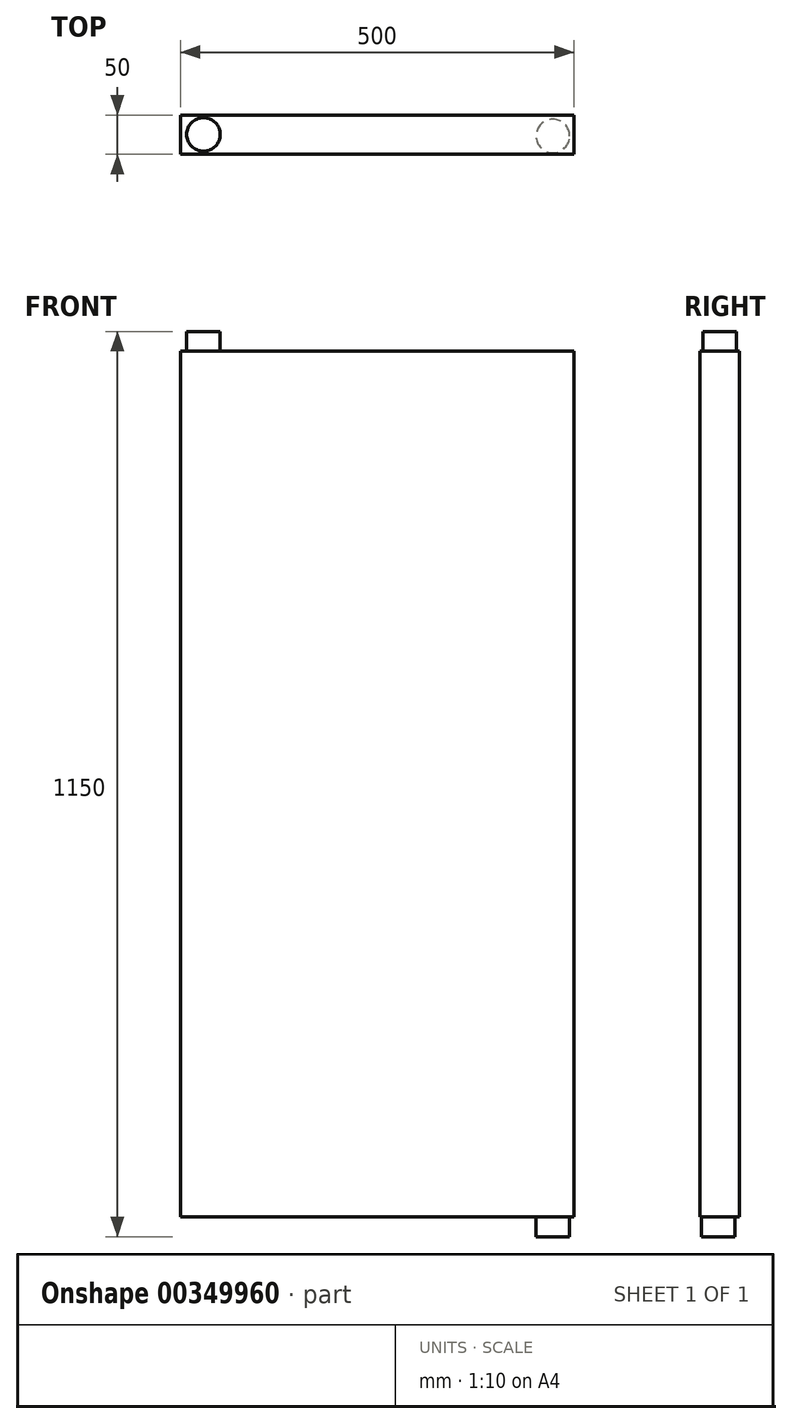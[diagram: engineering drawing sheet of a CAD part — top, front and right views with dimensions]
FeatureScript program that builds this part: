
annotation { "Feature Type Name" : "Feature", "Feature Type Description" : "" }
export const myFeature = defineFeature(function(context is Context, id is Id, definition is map)
    precondition{}
    {
        {
            var Q0;
            Q0=qCreatedBy(makeId("Front.planeOp"),FACE);
            var sketch = newSketch(context, id + "F0", { "sketchPlane" : qUnion([Q0])});
            skLineSegment(sketch, "E0.bottom", {"start": v(250, -550) * mm, "end": v(-250, -550) * mm});
            skLineSegment(sketch, "E0.top", {"start": v(250, 550) * mm, "end": v(-250, 550) * mm});
            skLineSegment(sketch, "E0.left", {"start": v(250, -550) * mm, "end": v(250, 550) * mm});
            skLineSegment(sketch, "E0.right", {"start": v(-250, -550) * mm, "end": v(-250, 550) * mm});
            skPoint(sketch, "E0.middle", {"position": v(0, 0) * mm});
            skSolve(sketch);
        }
        {
            var Q0;
            Q0 = qSketchRegion(id + "F0", true);
            extrude(context, id + "F1", {"entities" : qUnion([Q0]), "depth" : 50 * mm, "offsetDistance" : 25 * mm});
        }
        {
            var Q0;
            Q0=makeQuery(id+"F1.opExtrude","SWEPT_FACE",FACE,{"disambiguationData":[OSD([sQuery(id+"F0.wireOp",EDGE,"E0.top")])]});
            var sketch = newSketch(context, id + "F2", { "sketchPlane" : qUnion([Q0])});
            skCircle(sketch, "E1", {"center": v(-220.65, -24.76) * mm, "radius": 21.31 * mm});
            skSolve(sketch);
        }
        {
            var Q0;
            Q0 = qSketchRegion(id + "F2", true);
            extrude(context, id + "F3", {"entities" : qUnion([Q0]), "operationType" : NewBodyOperationType.ADD, "depth" : 25 * mm, "offsetDistance" : 25 * mm});
        }
        {
            var Q0;
            Q0=makeQuery(id+"F1.opExtrude","SWEPT_FACE",FACE,{"disambiguationData":[OSD([sQuery(id+"F0.wireOp",EDGE,"E0.bottom")])]});
            var sketch = newSketch(context, id + "F4", { "sketchPlane" : qUnion([Q0])});
            skCircle(sketch, "E2", {"center": v(223.22, 26.81) * mm, "radius": 21.29 * mm});
            skSolve(sketch);
        }
        {
            var Q0;
            Q0 = qSketchRegion(id + "F4", true);
            extrude(context, id + "F5", {"entities" : qUnion([Q0]), "operationType" : NewBodyOperationType.ADD, "depth" : 25 * mm, "offsetDistance" : 25 * mm});
        }
    });
